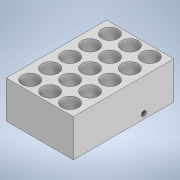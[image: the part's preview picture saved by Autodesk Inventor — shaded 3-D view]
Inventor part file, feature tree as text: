
AUTODESK INVENTOR PART (.ipt)
format: ipt  version: 2020 (Build 240168000, 168)  size: 194,048 bytes
history: native  units: in
note: dims shown in document units (in); Inventor stores cm internally (conversion verified against a paired STEP export)
features: sketch x6, hole x5, extrude x1, pattern_linear x1
ambient origin geometry x8: Origin, YZ Plane, XZ Plane, XY Plane, X Axis, Y Axis, Z Axis, Center Point
bodies: Solid1 (feature_tree)
feature tree (13):
  extrude  "Extrusion1"  Depth=5.0299in
  hole  "Hole1"  [1 undecoded]
  hole  "Hole2"  [1 undecoded]
  pattern_linear  "Rectangular Pattern1"  Spacing1=1.878in  [1 undecoded]
  hole  "Hole3"  [1 undecoded]
  hole  "Hole4"  [1 undecoded]
  hole  "Hole5"  [1 undecoded]
  sketch  "Sketch1"  dims[d0=3.3654in d1=5.0299in]
  sketch  "Sketch2"  dims[d2=1.0in d3=135.0deg]
  sketch  "Sketch4"  dims[d4=1.0in d5=1.0in]
  sketch  "Sketch5"  dims[d6=135.0deg]
  sketch  "Sketch6"  dims[d7=1.0in]
  sketch  "Sketch7"  dims[d8=45.0deg d9=1.878in d10=0.0in d11=1.0in d12=135.0deg d13=1.0in d14=135.0deg d15=1.0in d16=45.0deg d17=1.0in d18=45.0deg d19=0.145in d20=0.25in d21=0.375in d22=0.19in d23=0.5635in d24=0.375in d25=0.8108in d28=0.8268in d29=0.25in d30=0.375in d31=0.25in d32=0.5635in d33=1.378in d34=0.0in d35=1.1811in d37=1.0in d38=1.9685in d40=1.0in d41=0.6825in d42=0.5165in d43=1.5in d44=0.25in d45=0.25in d46=0.25in d47=0.119in d48=0.25in d49=0.5635in d50=1.25in d51=0.8108in d52=0.25in d53=0.125in d54=0.25in d55=0.119in d56=0.25in d57=0.5635in d58=2.0in d59=0.8108in d60=1.5in d61=0.25in d62=0.25in d63=0.25in d64=0.119in d65=0.25in d66=0.5635in d67=1.25in d68=0.8108in]
note: 6 required parameter values undecoded (feature->parameter linkage not recoverable at this tier; creation-order binding heuristic only, values carry confidence <= 0.55)
